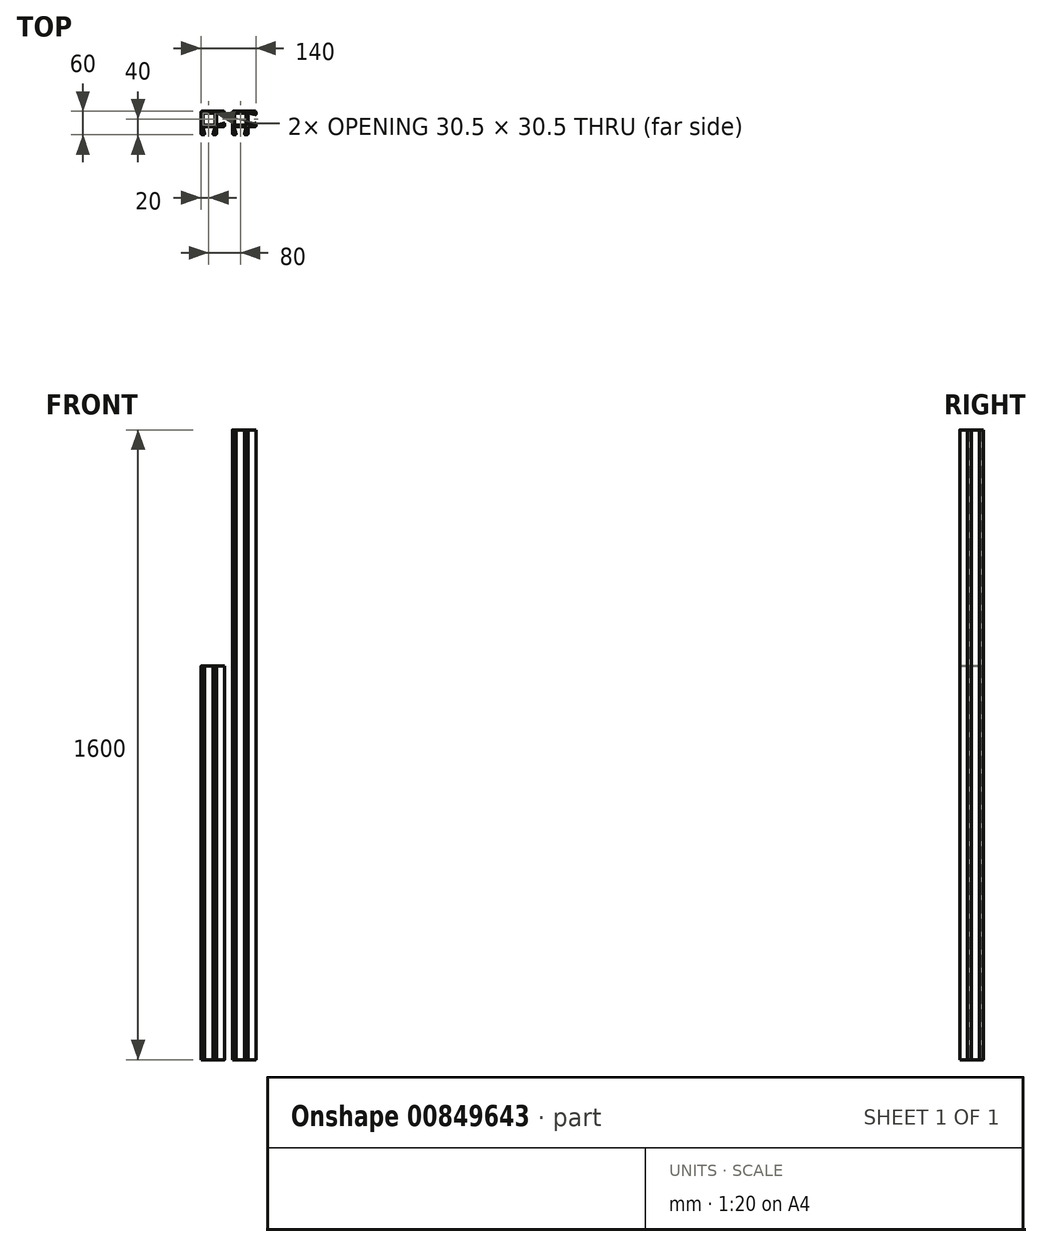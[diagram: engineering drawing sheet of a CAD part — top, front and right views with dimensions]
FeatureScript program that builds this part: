
annotation { "Feature Type Name" : "Feature", "Feature Type Description" : "" }
export const myFeature = defineFeature(function(context is Context, id is Id, definition is map)
    precondition{}
    {
        {
            var Q0;
            Q0=qCreatedBy(makeId("Top.planeOp"),FACE);
            var sketch = newSketch(context, id + "F0", { "sketchPlane" : qUnion([Q0])});
            skLineSegment(sketch, "E0", {"start": v(28.43, -0.67) * mm, "end": v(11.26, -5.27) * mm});
            skLineSegment(sketch, "E1", {"start": v(30, -6) * mm, "end": v(30, -1.88) * mm});
            skLineSegment(sketch, "E2", {"start": v(14, -10) * mm, "end": v(26, -10) * mm});
            skLineSegment(sketch, "E3", {"start": v(10, -26) * mm, "end": v(10, -14) * mm});
            skLineSegment(sketch, "E4", {"start": v(1.88, -30) * mm, "end": v(6, -30) * mm});
            skLineSegment(sketch, "E5", {"start": v(5.27, -11.26) * mm, "end": v(0.67, -28.43) * mm});
            skLineSegment(sketch, "E6", {"start": v(-9, -10) * mm, "end": v(4.3, -10) * mm});
            skLineSegment(sketch, "E7", {"start": v(-9.75, -9.64) * mm, "end": v(-9.25, -9.93) * mm});
            skLineSegment(sketch, "E8", {"start": v(-10.75, -9.93) * mm, "end": v(-10.25, -9.64) * mm});
            skLineSegment(sketch, "E9", {"start": v(-24.3, -10) * mm, "end": v(-11, -10) * mm});
            skLineSegment(sketch, "E10", {"start": v(-20.67, -28.43) * mm, "end": v(-25.27, -11.26) * mm});
            skLineSegment(sketch, "E11", {"start": v(-26, -30) * mm, "end": v(-21.88, -30) * mm});
            skLineSegment(sketch, "E12", {"start": v(-30, 26) * mm, "end": v(-30, -26) * mm});
            skLineSegment(sketch, "E13", {"start": v(26, 30) * mm, "end": v(-26, 30) * mm});
            skLineSegment(sketch, "E14", {"start": v(30, 21.88) * mm, "end": v(30, 26) * mm});
            skLineSegment(sketch, "E15", {"start": v(11.26, 25.27) * mm, "end": v(28.43, 20.67) * mm});
            skLineSegment(sketch, "E16", {"start": v(10, 11) * mm, "end": v(10, 24.3) * mm});
            skLineSegment(sketch, "E17", {"start": v(9.93, 10.75) * mm, "end": v(9.64, 10.25) * mm});
            skLineSegment(sketch, "E18", {"start": v(9.64, 9.75) * mm, "end": v(9.93, 9.25) * mm});
            skLineSegment(sketch, "E19", {"start": v(10, -4.3) * mm, "end": v(10, 9) * mm});
            skLineSegment(sketch, "E20", {"start": v(5.25, -4.75) * mm, "end": v(5.25, 24.75) * mm});
            skLineSegment(sketch, "E21", {"start": v(4.75, 25.25) * mm, "end": v(-24.75, 25.25) * mm});
            skLineSegment(sketch, "E22", {"start": v(-25.25, 24.75) * mm, "end": v(-25.25, -4.75) * mm});
            skLineSegment(sketch, "E23", {"start": v(-24.75, -5.25) * mm, "end": v(4.75, -5.25) * mm});
            skArc(sketch, "E24", {"start": v(10, -4.3) * mm, "mid": v(10.4, -5.1) * mm, "end": v(11.26, -5.27) * mm});
            skArc(sketch, "E25", {"start": v(30, -1.88) * mm, "mid": v(29.51, -0.89) * mm, "end": v(28.43, -0.67) * mm});
            skArc(sketch, "E26", {"start": v(26, -10) * mm, "mid": v(28.83, -8.83) * mm, "end": v(30, -6) * mm});
            skArc(sketch, "E27", {"start": v(14, -10) * mm, "mid": v(11.17, -11.17) * mm, "end": v(10, -14) * mm});
            skArc(sketch, "E28", {"start": v(6, -30) * mm, "mid": v(8.83, -28.83) * mm, "end": v(10, -26) * mm});
            skArc(sketch, "E29", {"start": v(0.67, -28.43) * mm, "mid": v(0.89, -29.51) * mm, "end": v(1.88, -30) * mm});
            skArc(sketch, "E30", {"start": v(5.27, -11.26) * mm, "mid": v(5.1, -10.4) * mm, "end": v(4.3, -10) * mm});
            skArc(sketch, "E31", {"start": v(-9.25, -9.93) * mm, "mid": v(-9.13, -9.98) * mm, "end": v(-9, -10) * mm});
            skArc(sketch, "E32", {"start": v(-9.75, -9.64) * mm, "mid": v(-10, -9.58) * mm, "end": v(-10.25, -9.64) * mm});
            skArc(sketch, "E33", {"start": v(-11, -10) * mm, "mid": v(-10.87, -9.98) * mm, "end": v(-10.75, -9.93) * mm});
            skArc(sketch, "E34", {"start": v(-24.3, -10) * mm, "mid": v(-25.1, -10.4) * mm, "end": v(-25.27, -11.26) * mm});
            skArc(sketch, "E35", {"start": v(-21.88, -30) * mm, "mid": v(-20.89, -29.51) * mm, "end": v(-20.67, -28.43) * mm});
            skArc(sketch, "E36", {"start": v(-30, -26) * mm, "mid": v(-28.83, -28.83) * mm, "end": v(-26, -30) * mm});
            skArc(sketch, "E37", {"start": v(-26, 30) * mm, "mid": v(-28.83, 28.83) * mm, "end": v(-30, 26) * mm});
            skArc(sketch, "E38", {"start": v(30, 26) * mm, "mid": v(28.83, 28.83) * mm, "end": v(26, 30) * mm});
            skArc(sketch, "E39", {"start": v(28.43, 20.67) * mm, "mid": v(29.51, 20.89) * mm, "end": v(30, 21.88) * mm});
            skArc(sketch, "E40", {"start": v(11.26, 25.27) * mm, "mid": v(10.4, 25.1) * mm, "end": v(10, 24.3) * mm});
            skArc(sketch, "E41", {"start": v(9.93, 10.75) * mm, "mid": v(9.98, 10.87) * mm, "end": v(10, 11) * mm});
            skArc(sketch, "E42", {"start": v(9.64, 10.25) * mm, "mid": v(9.58, 10) * mm, "end": v(9.64, 9.75) * mm});
            skArc(sketch, "E43", {"start": v(10, 9) * mm, "mid": v(9.98, 9.13) * mm, "end": v(9.93, 9.25) * mm});
            skArc(sketch, "E44", {"start": v(4.75, -5.25) * mm, "mid": v(5.1, -5.1) * mm, "end": v(5.25, -4.75) * mm});
            skArc(sketch, "E45", {"start": v(5.25, 24.75) * mm, "mid": v(5.1, 25.1) * mm, "end": v(4.75, 25.25) * mm});
            skArc(sketch, "E46", {"start": v(-24.75, 25.25) * mm, "mid": v(-25.1, 25.1) * mm, "end": v(-25.25, 24.75) * mm});
            skArc(sketch, "E47", {"start": v(-25.25, -4.75) * mm, "mid": v(-25.1, -5.1) * mm, "end": v(-24.75, -5.25) * mm});
            skLineSegment(sketch, "E48.1.0.0", {"start": v(108.43, -0.67) * mm, "end": v(91.26, -5.27) * mm});
            skLineSegment(sketch, "E48.1.0.1", {"start": v(94, -10) * mm, "end": v(106, -10) * mm});
            skLineSegment(sketch, "E48.1.0.2", {"start": v(55.25, -5.25) * mm, "end": v(84.75, -5.25) * mm});
            skLineSegment(sketch, "E48.1.0.3", {"start": v(54.75, 24.75) * mm, "end": v(54.75, -4.75) * mm});
            skLineSegment(sketch, "E48.1.0.4", {"start": v(84.75, 25.25) * mm, "end": v(55.25, 25.25) * mm});
            skLineSegment(sketch, "E48.1.0.5", {"start": v(71, -10) * mm, "end": v(84.3, -10) * mm});
            skLineSegment(sketch, "E48.1.0.6", {"start": v(85.25, -4.75) * mm, "end": v(85.25, 24.75) * mm});
            skLineSegment(sketch, "E48.1.0.7", {"start": v(50, 26) * mm, "end": v(50, -26) * mm});
            skLineSegment(sketch, "E48.1.0.8", {"start": v(91.26, 25.27) * mm, "end": v(108.43, 20.67) * mm});
            skLineSegment(sketch, "E48.1.0.9", {"start": v(106, 30) * mm, "end": v(54, 30) * mm});
            skLineSegment(sketch, "E48.1.0.10", {"start": v(85.27, -11.26) * mm, "end": v(80.67, -28.43) * mm});
            skArc(sketch, "E48.1.0.11", {"start": v(86, -30) * mm, "mid": v(88.83, -28.83) * mm, "end": v(90, -26) * mm});
            skArc(sketch, "E48.1.0.12", {"start": v(106, -10) * mm, "mid": v(108.83, -8.83) * mm, "end": v(110, -6) * mm});
            skLineSegment(sketch, "E48.1.0.13", {"start": v(90, -26) * mm, "end": v(90, -14) * mm});
            skArc(sketch, "E48.1.0.14", {"start": v(108.43, 20.67) * mm, "mid": v(109.51, 20.89) * mm, "end": v(110, 21.88) * mm});
            skArc(sketch, "E48.1.0.15", {"start": v(110, 26) * mm, "mid": v(108.83, 28.83) * mm, "end": v(106, 30) * mm});
            skArc(sketch, "E48.1.0.16", {"start": v(50, -26) * mm, "mid": v(51.17, -28.83) * mm, "end": v(54, -30) * mm});
            skLineSegment(sketch, "E48.1.0.17", {"start": v(110, 21.88) * mm, "end": v(110, 26) * mm});
            skArc(sketch, "E48.1.0.18", {"start": v(91.26, 25.27) * mm, "mid": v(90.4, 25.1) * mm, "end": v(90, 24.3) * mm});
            skArc(sketch, "E48.1.0.19", {"start": v(55.25, 25.25) * mm, "mid": v(54.9, 25.1) * mm, "end": v(54.75, 24.75) * mm});
            skArc(sketch, "E48.1.0.20", {"start": v(54, 30) * mm, "mid": v(51.17, 28.83) * mm, "end": v(50, 26) * mm});
            skLineSegment(sketch, "E48.1.0.21", {"start": v(59.33, -28.43) * mm, "end": v(54.73, -11.26) * mm});
            skLineSegment(sketch, "E48.1.0.22", {"start": v(54, -30) * mm, "end": v(58.12, -30) * mm});
            skArc(sketch, "E48.1.0.23", {"start": v(94, -10) * mm, "mid": v(91.17, -11.17) * mm, "end": v(90, -14) * mm});
            skArc(sketch, "E48.1.0.24", {"start": v(90, -4.3) * mm, "mid": v(90.4, -5.1) * mm, "end": v(91.26, -5.27) * mm});
            skArc(sketch, "E48.1.0.25", {"start": v(54.75, -4.75) * mm, "mid": v(54.9, -5.1) * mm, "end": v(55.25, -5.25) * mm});
            skArc(sketch, "E48.1.0.26", {"start": v(58.12, -30) * mm, "mid": v(59.11, -29.51) * mm, "end": v(59.33, -28.43) * mm});
            skLineSegment(sketch, "E48.1.0.27", {"start": v(90, -4.3) * mm, "end": v(90, 9) * mm});
            skArc(sketch, "E48.1.0.28", {"start": v(55.7, -10) * mm, "mid": v(54.9, -10.4) * mm, "end": v(54.73, -11.26) * mm});
            skLineSegment(sketch, "E48.1.0.29", {"start": v(55.7, -10) * mm, "end": v(69, -10) * mm});
            skLineSegment(sketch, "E48.1.0.30", {"start": v(90, 11) * mm, "end": v(90, 24.3) * mm});
            skArc(sketch, "E48.1.0.31", {"start": v(84.75, -5.25) * mm, "mid": v(85.1, -5.1) * mm, "end": v(85.25, -4.75) * mm});
            skArc(sketch, "E48.1.0.32", {"start": v(110, -1.88) * mm, "mid": v(109.51, -0.89) * mm, "end": v(108.43, -0.67) * mm});
            skLineSegment(sketch, "E48.1.0.33", {"start": v(110, -6) * mm, "end": v(110, -1.88) * mm});
            skLineSegment(sketch, "E48.1.0.34", {"start": v(81.88, -30) * mm, "end": v(86, -30) * mm});
            skArc(sketch, "E48.1.0.35", {"start": v(85.27, -11.26) * mm, "mid": v(85.1, -10.4) * mm, "end": v(84.3, -10) * mm});
            skArc(sketch, "E48.1.0.36", {"start": v(85.25, 24.75) * mm, "mid": v(85.1, 25.1) * mm, "end": v(84.75, 25.25) * mm});
            skArc(sketch, "E48.1.0.37", {"start": v(80.67, -28.43) * mm, "mid": v(80.89, -29.51) * mm, "end": v(81.88, -30) * mm});
            skLineSegment(sketch, "E48.1.0.38", {"start": v(69.25, -9.93) * mm, "end": v(69.75, -9.64) * mm});
            skArc(sketch, "E48.1.0.39", {"start": v(70.25, -9.64) * mm, "mid": v(70, -9.58) * mm, "end": v(69.75, -9.64) * mm});
            skArc(sketch, "E48.1.0.40", {"start": v(70.75, -9.93) * mm, "mid": v(70.87, -9.98) * mm, "end": v(71, -10) * mm});
            skLineSegment(sketch, "E48.1.0.41", {"start": v(89.64, 9.75) * mm, "end": v(89.93, 9.25) * mm});
            skArc(sketch, "E48.1.0.42", {"start": v(69, -10) * mm, "mid": v(69.13, -9.98) * mm, "end": v(69.25, -9.93) * mm});
            skLineSegment(sketch, "E48.1.0.43", {"start": v(89.93, 10.75) * mm, "end": v(89.64, 10.25) * mm});
            skArc(sketch, "E48.1.0.44", {"start": v(89.64, 10.25) * mm, "mid": v(89.58, 10) * mm, "end": v(89.64, 9.75) * mm});
            skArc(sketch, "E48.1.0.45", {"start": v(89.93, 10.75) * mm, "mid": v(89.98, 10.87) * mm, "end": v(90, 11) * mm});
            skLineSegment(sketch, "E48.1.0.46", {"start": v(70.25, -9.64) * mm, "end": v(70.75, -9.93) * mm});
            skArc(sketch, "E48.1.0.47", {"start": v(90, 9) * mm, "mid": v(89.98, 9.13) * mm, "end": v(89.93, 9.25) * mm});
            skLineSegment(sketch, "E48.2.0.0", {"start": v(188.43, -0.67) * mm, "end": v(171.26, -5.27) * mm});
            skLineSegment(sketch, "E48.2.0.1", {"start": v(174, -10) * mm, "end": v(186, -10) * mm});
            skLineSegment(sketch, "E48.2.0.2", {"start": v(135.25, -5.25) * mm, "end": v(164.75, -5.25) * mm});
            skLineSegment(sketch, "E48.2.0.3", {"start": v(134.75, 24.75) * mm, "end": v(134.75, -4.75) * mm});
            skLineSegment(sketch, "E48.2.0.4", {"start": v(164.75, 25.25) * mm, "end": v(135.25, 25.25) * mm});
            skLineSegment(sketch, "E48.2.0.5", {"start": v(151, -10) * mm, "end": v(164.3, -10) * mm});
            skLineSegment(sketch, "E48.2.0.6", {"start": v(165.25, -4.75) * mm, "end": v(165.25, 24.75) * mm});
            skLineSegment(sketch, "E48.2.0.7", {"start": v(130, 26) * mm, "end": v(130, -26) * mm});
            skLineSegment(sketch, "E48.2.0.8", {"start": v(171.26, 25.27) * mm, "end": v(188.43, 20.67) * mm});
            skLineSegment(sketch, "E48.2.0.9", {"start": v(186, 30) * mm, "end": v(134, 30) * mm});
            skLineSegment(sketch, "E48.2.0.10", {"start": v(165.27, -11.26) * mm, "end": v(160.67, -28.43) * mm});
            skArc(sketch, "E48.2.0.11", {"start": v(166, -30) * mm, "mid": v(168.83, -28.83) * mm, "end": v(170, -26) * mm});
            skArc(sketch, "E48.2.0.12", {"start": v(186, -10) * mm, "mid": v(188.83, -8.83) * mm, "end": v(190, -6) * mm});
            skLineSegment(sketch, "E48.2.0.13", {"start": v(170, -26) * mm, "end": v(170, -14) * mm});
            skArc(sketch, "E48.2.0.14", {"start": v(188.43, 20.67) * mm, "mid": v(189.51, 20.89) * mm, "end": v(190, 21.88) * mm});
            skArc(sketch, "E48.2.0.15", {"start": v(190, 26) * mm, "mid": v(188.83, 28.83) * mm, "end": v(186, 30) * mm});
            skArc(sketch, "E48.2.0.16", {"start": v(130, -26) * mm, "mid": v(131.17, -28.83) * mm, "end": v(134, -30) * mm});
            skLineSegment(sketch, "E48.2.0.17", {"start": v(190, 21.88) * mm, "end": v(190, 26) * mm});
            skArc(sketch, "E48.2.0.18", {"start": v(171.26, 25.27) * mm, "mid": v(170.4, 25.1) * mm, "end": v(170, 24.3) * mm});
            skArc(sketch, "E48.2.0.19", {"start": v(135.25, 25.25) * mm, "mid": v(134.9, 25.1) * mm, "end": v(134.75, 24.75) * mm});
            skArc(sketch, "E48.2.0.20", {"start": v(134, 30) * mm, "mid": v(131.17, 28.83) * mm, "end": v(130, 26) * mm});
            skLineSegment(sketch, "E48.2.0.21", {"start": v(139.33, -28.43) * mm, "end": v(134.73, -11.26) * mm});
            skLineSegment(sketch, "E48.2.0.22", {"start": v(134, -30) * mm, "end": v(138.12, -30) * mm});
            skArc(sketch, "E48.2.0.23", {"start": v(174, -10) * mm, "mid": v(171.17, -11.17) * mm, "end": v(170, -14) * mm});
            skArc(sketch, "E48.2.0.24", {"start": v(170, -4.3) * mm, "mid": v(170.4, -5.1) * mm, "end": v(171.26, -5.27) * mm});
            skArc(sketch, "E48.2.0.25", {"start": v(134.75, -4.75) * mm, "mid": v(134.9, -5.1) * mm, "end": v(135.25, -5.25) * mm});
            skArc(sketch, "E48.2.0.26", {"start": v(138.12, -30) * mm, "mid": v(139.11, -29.51) * mm, "end": v(139.33, -28.43) * mm});
            skLineSegment(sketch, "E48.2.0.27", {"start": v(170, -4.3) * mm, "end": v(170, 9) * mm});
            skArc(sketch, "E48.2.0.28", {"start": v(135.7, -10) * mm, "mid": v(134.9, -10.4) * mm, "end": v(134.73, -11.26) * mm});
            skLineSegment(sketch, "E48.2.0.29", {"start": v(135.7, -10) * mm, "end": v(149, -10) * mm});
            skLineSegment(sketch, "E48.2.0.30", {"start": v(170, 11) * mm, "end": v(170, 24.3) * mm});
            skArc(sketch, "E48.2.0.31", {"start": v(164.75, -5.25) * mm, "mid": v(165.1, -5.1) * mm, "end": v(165.25, -4.75) * mm});
            skArc(sketch, "E48.2.0.32", {"start": v(190, -1.88) * mm, "mid": v(189.51, -0.89) * mm, "end": v(188.43, -0.67) * mm});
            skLineSegment(sketch, "E48.2.0.33", {"start": v(190, -6) * mm, "end": v(190, -1.88) * mm});
            skLineSegment(sketch, "E48.2.0.34", {"start": v(161.88, -30) * mm, "end": v(166, -30) * mm});
            skArc(sketch, "E48.2.0.35", {"start": v(165.27, -11.26) * mm, "mid": v(165.1, -10.4) * mm, "end": v(164.3, -10) * mm});
            skArc(sketch, "E48.2.0.36", {"start": v(165.25, 24.75) * mm, "mid": v(165.1, 25.1) * mm, "end": v(164.75, 25.25) * mm});
            skArc(sketch, "E48.2.0.37", {"start": v(160.67, -28.43) * mm, "mid": v(160.89, -29.51) * mm, "end": v(161.88, -30) * mm});
            skLineSegment(sketch, "E48.2.0.38", {"start": v(149.25, -9.93) * mm, "end": v(149.75, -9.64) * mm});
            skArc(sketch, "E48.2.0.39", {"start": v(150.25, -9.64) * mm, "mid": v(150, -9.58) * mm, "end": v(149.75, -9.64) * mm});
            skArc(sketch, "E48.2.0.40", {"start": v(150.75, -9.93) * mm, "mid": v(150.87, -9.98) * mm, "end": v(151, -10) * mm});
            skLineSegment(sketch, "E48.2.0.41", {"start": v(169.64, 9.75) * mm, "end": v(169.93, 9.25) * mm});
            skArc(sketch, "E48.2.0.42", {"start": v(149, -10) * mm, "mid": v(149.13, -9.98) * mm, "end": v(149.25, -9.93) * mm});
            skLineSegment(sketch, "E48.2.0.43", {"start": v(169.93, 10.75) * mm, "end": v(169.64, 10.25) * mm});
            skArc(sketch, "E48.2.0.44", {"start": v(169.64, 10.25) * mm, "mid": v(169.58, 10) * mm, "end": v(169.64, 9.75) * mm});
            skArc(sketch, "E48.2.0.45", {"start": v(169.93, 10.75) * mm, "mid": v(169.98, 10.87) * mm, "end": v(170, 11) * mm});
            skLineSegment(sketch, "E48.2.0.46", {"start": v(150.25, -9.64) * mm, "end": v(150.75, -9.93) * mm});
            skArc(sketch, "E48.2.0.47", {"start": v(170, 9) * mm, "mid": v(169.98, 9.13) * mm, "end": v(169.93, 9.25) * mm});
            skLineSegment(sketch, "E48.3.0.0", {"start": v(268.43, -0.67) * mm, "end": v(251.26, -5.27) * mm});
            skLineSegment(sketch, "E48.3.0.1", {"start": v(254, -10) * mm, "end": v(266, -10) * mm});
            skLineSegment(sketch, "E48.3.0.2", {"start": v(215.25, -5.25) * mm, "end": v(244.75, -5.25) * mm});
            skLineSegment(sketch, "E48.3.0.3", {"start": v(214.75, 24.75) * mm, "end": v(214.75, -4.75) * mm});
            skLineSegment(sketch, "E48.3.0.4", {"start": v(244.75, 25.25) * mm, "end": v(215.25, 25.25) * mm});
            skLineSegment(sketch, "E48.3.0.5", {"start": v(231, -10) * mm, "end": v(244.3, -10) * mm});
            skLineSegment(sketch, "E48.3.0.6", {"start": v(245.25, -4.75) * mm, "end": v(245.25, 24.75) * mm});
            skLineSegment(sketch, "E48.3.0.7", {"start": v(210, 26) * mm, "end": v(210, -26) * mm});
            skLineSegment(sketch, "E48.3.0.8", {"start": v(251.26, 25.27) * mm, "end": v(268.43, 20.67) * mm});
            skLineSegment(sketch, "E48.3.0.9", {"start": v(266, 30) * mm, "end": v(214, 30) * mm});
            skLineSegment(sketch, "E48.3.0.10", {"start": v(245.27, -11.26) * mm, "end": v(240.67, -28.43) * mm});
            skArc(sketch, "E48.3.0.11", {"start": v(246, -30) * mm, "mid": v(248.83, -28.83) * mm, "end": v(250, -26) * mm});
            skArc(sketch, "E48.3.0.12", {"start": v(266, -10) * mm, "mid": v(268.83, -8.83) * mm, "end": v(270, -6) * mm});
            skLineSegment(sketch, "E48.3.0.13", {"start": v(250, -26) * mm, "end": v(250, -14) * mm});
            skArc(sketch, "E48.3.0.14", {"start": v(268.43, 20.67) * mm, "mid": v(269.51, 20.89) * mm, "end": v(270, 21.88) * mm});
            skArc(sketch, "E48.3.0.15", {"start": v(270, 26) * mm, "mid": v(268.83, 28.83) * mm, "end": v(266, 30) * mm});
            skArc(sketch, "E48.3.0.16", {"start": v(210, -26) * mm, "mid": v(211.17, -28.83) * mm, "end": v(214, -30) * mm});
            skLineSegment(sketch, "E48.3.0.17", {"start": v(270, 21.88) * mm, "end": v(270, 26) * mm});
            skArc(sketch, "E48.3.0.18", {"start": v(251.26, 25.27) * mm, "mid": v(250.4, 25.1) * mm, "end": v(250, 24.3) * mm});
            skArc(sketch, "E48.3.0.19", {"start": v(215.25, 25.25) * mm, "mid": v(214.9, 25.1) * mm, "end": v(214.75, 24.75) * mm});
            skArc(sketch, "E48.3.0.20", {"start": v(214, 30) * mm, "mid": v(211.17, 28.83) * mm, "end": v(210, 26) * mm});
            skLineSegment(sketch, "E48.3.0.21", {"start": v(219.33, -28.43) * mm, "end": v(214.73, -11.26) * mm});
            skLineSegment(sketch, "E48.3.0.22", {"start": v(214, -30) * mm, "end": v(218.12, -30) * mm});
            skArc(sketch, "E48.3.0.23", {"start": v(254, -10) * mm, "mid": v(251.17, -11.17) * mm, "end": v(250, -14) * mm});
            skArc(sketch, "E48.3.0.24", {"start": v(250, -4.3) * mm, "mid": v(250.4, -5.1) * mm, "end": v(251.26, -5.27) * mm});
            skArc(sketch, "E48.3.0.25", {"start": v(214.75, -4.75) * mm, "mid": v(214.9, -5.1) * mm, "end": v(215.25, -5.25) * mm});
            skArc(sketch, "E48.3.0.26", {"start": v(218.12, -30) * mm, "mid": v(219.11, -29.51) * mm, "end": v(219.33, -28.43) * mm});
            skLineSegment(sketch, "E48.3.0.27", {"start": v(250, -4.3) * mm, "end": v(250, 9) * mm});
            skArc(sketch, "E48.3.0.28", {"start": v(215.7, -10) * mm, "mid": v(214.9, -10.4) * mm, "end": v(214.73, -11.26) * mm});
            skLineSegment(sketch, "E48.3.0.29", {"start": v(215.7, -10) * mm, "end": v(229, -10) * mm});
            skLineSegment(sketch, "E48.3.0.30", {"start": v(250, 11) * mm, "end": v(250, 24.3) * mm});
            skArc(sketch, "E48.3.0.31", {"start": v(244.75, -5.25) * mm, "mid": v(245.1, -5.1) * mm, "end": v(245.25, -4.75) * mm});
            skArc(sketch, "E48.3.0.32", {"start": v(270, -1.88) * mm, "mid": v(269.51, -0.89) * mm, "end": v(268.43, -0.67) * mm});
            skLineSegment(sketch, "E48.3.0.33", {"start": v(270, -6) * mm, "end": v(270, -1.88) * mm});
            skLineSegment(sketch, "E48.3.0.34", {"start": v(241.88, -30) * mm, "end": v(246, -30) * mm});
            skArc(sketch, "E48.3.0.35", {"start": v(245.27, -11.26) * mm, "mid": v(245.1, -10.4) * mm, "end": v(244.3, -10) * mm});
            skArc(sketch, "E48.3.0.36", {"start": v(245.25, 24.75) * mm, "mid": v(245.1, 25.1) * mm, "end": v(244.75, 25.25) * mm});
            skArc(sketch, "E48.3.0.37", {"start": v(240.67, -28.43) * mm, "mid": v(240.89, -29.51) * mm, "end": v(241.88, -30) * mm});
            skLineSegment(sketch, "E48.3.0.38", {"start": v(229.25, -9.93) * mm, "end": v(229.75, -9.64) * mm});
            skArc(sketch, "E48.3.0.39", {"start": v(230.25, -9.64) * mm, "mid": v(230, -9.58) * mm, "end": v(229.75, -9.64) * mm});
            skArc(sketch, "E48.3.0.40", {"start": v(230.75, -9.93) * mm, "mid": v(230.87, -9.98) * mm, "end": v(231, -10) * mm});
            skLineSegment(sketch, "E48.3.0.41", {"start": v(249.64, 9.75) * mm, "end": v(249.93, 9.25) * mm});
            skArc(sketch, "E48.3.0.42", {"start": v(229, -10) * mm, "mid": v(229.13, -9.98) * mm, "end": v(229.25, -9.93) * mm});
            skLineSegment(sketch, "E48.3.0.43", {"start": v(249.93, 10.75) * mm, "end": v(249.64, 10.25) * mm});
            skArc(sketch, "E48.3.0.44", {"start": v(249.64, 10.25) * mm, "mid": v(249.58, 10) * mm, "end": v(249.64, 9.75) * mm});
            skArc(sketch, "E48.3.0.45", {"start": v(249.93, 10.75) * mm, "mid": v(249.98, 10.87) * mm, "end": v(250, 11) * mm});
            skLineSegment(sketch, "E48.3.0.46", {"start": v(230.25, -9.64) * mm, "end": v(230.75, -9.93) * mm});
            skArc(sketch, "E48.3.0.47", {"start": v(250, 9) * mm, "mid": v(249.98, 9.13) * mm, "end": v(249.93, 9.25) * mm});
            skLineSegment(sketch, "E48.4.0.0", {"start": v(348.43, -0.67) * mm, "end": v(331.26, -5.27) * mm});
            skLineSegment(sketch, "E48.4.0.1", {"start": v(334, -10) * mm, "end": v(346, -10) * mm});
            skLineSegment(sketch, "E48.4.0.2", {"start": v(295.25, -5.25) * mm, "end": v(324.75, -5.25) * mm});
            skLineSegment(sketch, "E48.4.0.3", {"start": v(294.75, 24.75) * mm, "end": v(294.75, -4.75) * mm});
            skLineSegment(sketch, "E48.4.0.4", {"start": v(324.75, 25.25) * mm, "end": v(295.25, 25.25) * mm});
            skLineSegment(sketch, "E48.4.0.5", {"start": v(311, -10) * mm, "end": v(324.3, -10) * mm});
            skLineSegment(sketch, "E48.4.0.6", {"start": v(325.25, -4.75) * mm, "end": v(325.25, 24.75) * mm});
            skLineSegment(sketch, "E48.4.0.7", {"start": v(290, 26) * mm, "end": v(290, -26) * mm});
            skLineSegment(sketch, "E48.4.0.8", {"start": v(331.26, 25.27) * mm, "end": v(348.43, 20.67) * mm});
            skLineSegment(sketch, "E48.4.0.9", {"start": v(346, 30) * mm, "end": v(294, 30) * mm});
            skLineSegment(sketch, "E48.4.0.10", {"start": v(325.27, -11.26) * mm, "end": v(320.67, -28.43) * mm});
            skArc(sketch, "E48.4.0.11", {"start": v(326, -30) * mm, "mid": v(328.83, -28.83) * mm, "end": v(330, -26) * mm});
            skArc(sketch, "E48.4.0.12", {"start": v(346, -10) * mm, "mid": v(348.83, -8.83) * mm, "end": v(350, -6) * mm});
            skLineSegment(sketch, "E48.4.0.13", {"start": v(330, -26) * mm, "end": v(330, -14) * mm});
            skArc(sketch, "E48.4.0.14", {"start": v(348.43, 20.67) * mm, "mid": v(349.51, 20.89) * mm, "end": v(350, 21.88) * mm});
            skArc(sketch, "E48.4.0.15", {"start": v(350, 26) * mm, "mid": v(348.83, 28.83) * mm, "end": v(346, 30) * mm});
            skArc(sketch, "E48.4.0.16", {"start": v(290, -26) * mm, "mid": v(291.17, -28.83) * mm, "end": v(294, -30) * mm});
            skLineSegment(sketch, "E48.4.0.17", {"start": v(350, 21.88) * mm, "end": v(350, 26) * mm});
            skArc(sketch, "E48.4.0.18", {"start": v(331.26, 25.27) * mm, "mid": v(330.4, 25.1) * mm, "end": v(330, 24.3) * mm});
            skArc(sketch, "E48.4.0.19", {"start": v(295.25, 25.25) * mm, "mid": v(294.9, 25.1) * mm, "end": v(294.75, 24.75) * mm});
            skArc(sketch, "E48.4.0.20", {"start": v(294, 30) * mm, "mid": v(291.17, 28.83) * mm, "end": v(290, 26) * mm});
            skLineSegment(sketch, "E48.4.0.21", {"start": v(299.33, -28.43) * mm, "end": v(294.73, -11.26) * mm});
            skLineSegment(sketch, "E48.4.0.22", {"start": v(294, -30) * mm, "end": v(298.12, -30) * mm});
            skArc(sketch, "E48.4.0.23", {"start": v(334, -10) * mm, "mid": v(331.17, -11.17) * mm, "end": v(330, -14) * mm});
            skArc(sketch, "E48.4.0.24", {"start": v(330, -4.3) * mm, "mid": v(330.4, -5.1) * mm, "end": v(331.26, -5.27) * mm});
            skArc(sketch, "E48.4.0.25", {"start": v(294.75, -4.75) * mm, "mid": v(294.9, -5.1) * mm, "end": v(295.25, -5.25) * mm});
            skArc(sketch, "E48.4.0.26", {"start": v(298.12, -30) * mm, "mid": v(299.11, -29.51) * mm, "end": v(299.33, -28.43) * mm});
            skLineSegment(sketch, "E48.4.0.27", {"start": v(330, -4.3) * mm, "end": v(330, 9) * mm});
            skArc(sketch, "E48.4.0.28", {"start": v(295.7, -10) * mm, "mid": v(294.9, -10.4) * mm, "end": v(294.73, -11.26) * mm});
            skLineSegment(sketch, "E48.4.0.29", {"start": v(295.7, -10) * mm, "end": v(309, -10) * mm});
            skLineSegment(sketch, "E48.4.0.30", {"start": v(330, 11) * mm, "end": v(330, 24.3) * mm});
            skArc(sketch, "E48.4.0.31", {"start": v(324.75, -5.25) * mm, "mid": v(325.1, -5.1) * mm, "end": v(325.25, -4.75) * mm});
            skArc(sketch, "E48.4.0.32", {"start": v(350, -1.88) * mm, "mid": v(349.51, -0.89) * mm, "end": v(348.43, -0.67) * mm});
            skLineSegment(sketch, "E48.4.0.33", {"start": v(350, -6) * mm, "end": v(350, -1.88) * mm});
            skLineSegment(sketch, "E48.4.0.34", {"start": v(321.88, -30) * mm, "end": v(326, -30) * mm});
            skArc(sketch, "E48.4.0.35", {"start": v(325.27, -11.26) * mm, "mid": v(325.1, -10.4) * mm, "end": v(324.3, -10) * mm});
            skArc(sketch, "E48.4.0.36", {"start": v(325.25, 24.75) * mm, "mid": v(325.1, 25.1) * mm, "end": v(324.75, 25.25) * mm});
            skArc(sketch, "E48.4.0.37", {"start": v(320.67, -28.43) * mm, "mid": v(320.89, -29.51) * mm, "end": v(321.88, -30) * mm});
            skLineSegment(sketch, "E48.4.0.38", {"start": v(309.25, -9.93) * mm, "end": v(309.75, -9.64) * mm});
            skArc(sketch, "E48.4.0.39", {"start": v(310.25, -9.64) * mm, "mid": v(310, -9.58) * mm, "end": v(309.75, -9.64) * mm});
            skArc(sketch, "E48.4.0.40", {"start": v(310.75, -9.93) * mm, "mid": v(310.87, -9.98) * mm, "end": v(311, -10) * mm});
            skLineSegment(sketch, "E48.4.0.41", {"start": v(329.64, 9.75) * mm, "end": v(329.93, 9.25) * mm});
            skArc(sketch, "E48.4.0.42", {"start": v(309, -10) * mm, "mid": v(309.13, -9.98) * mm, "end": v(309.25, -9.93) * mm});
            skLineSegment(sketch, "E48.4.0.43", {"start": v(329.93, 10.75) * mm, "end": v(329.64, 10.25) * mm});
            skArc(sketch, "E48.4.0.44", {"start": v(329.64, 10.25) * mm, "mid": v(329.58, 10) * mm, "end": v(329.64, 9.75) * mm});
            skArc(sketch, "E48.4.0.45", {"start": v(329.93, 10.75) * mm, "mid": v(329.98, 10.87) * mm, "end": v(330, 11) * mm});
            skLineSegment(sketch, "E48.4.0.46", {"start": v(310.25, -9.64) * mm, "end": v(310.75, -9.93) * mm});
            skArc(sketch, "E48.4.0.47", {"start": v(330, 9) * mm, "mid": v(329.98, 9.13) * mm, "end": v(329.93, 9.25) * mm});
            skLineSegment(sketch, "E48.5.0.0", {"start": v(428.43, -0.67) * mm, "end": v(411.26, -5.27) * mm});
            skLineSegment(sketch, "E48.5.0.1", {"start": v(414, -10) * mm, "end": v(426, -10) * mm});
            skLineSegment(sketch, "E48.5.0.2", {"start": v(375.25, -5.25) * mm, "end": v(404.75, -5.25) * mm});
            skLineSegment(sketch, "E48.5.0.3", {"start": v(374.75, 24.75) * mm, "end": v(374.75, -4.75) * mm});
            skLineSegment(sketch, "E48.5.0.4", {"start": v(404.75, 25.25) * mm, "end": v(375.25, 25.25) * mm});
            skLineSegment(sketch, "E48.5.0.5", {"start": v(391, -10) * mm, "end": v(404.3, -10) * mm});
            skLineSegment(sketch, "E48.5.0.6", {"start": v(405.25, -4.75) * mm, "end": v(405.25, 24.75) * mm});
            skLineSegment(sketch, "E48.5.0.7", {"start": v(370, 26) * mm, "end": v(370, -26) * mm});
            skLineSegment(sketch, "E48.5.0.8", {"start": v(411.26, 25.27) * mm, "end": v(428.43, 20.67) * mm});
            skLineSegment(sketch, "E48.5.0.9", {"start": v(426, 30) * mm, "end": v(374, 30) * mm});
            skLineSegment(sketch, "E48.5.0.10", {"start": v(405.27, -11.26) * mm, "end": v(400.67, -28.43) * mm});
            skArc(sketch, "E48.5.0.11", {"start": v(406, -30) * mm, "mid": v(408.83, -28.83) * mm, "end": v(410, -26) * mm});
            skArc(sketch, "E48.5.0.12", {"start": v(426, -10) * mm, "mid": v(428.83, -8.83) * mm, "end": v(430, -6) * mm});
            skLineSegment(sketch, "E48.5.0.13", {"start": v(410, -26) * mm, "end": v(410, -14) * mm});
            skArc(sketch, "E48.5.0.14", {"start": v(428.43, 20.67) * mm, "mid": v(429.51, 20.89) * mm, "end": v(430, 21.88) * mm});
            skArc(sketch, "E48.5.0.15", {"start": v(430, 26) * mm, "mid": v(428.83, 28.83) * mm, "end": v(426, 30) * mm});
            skArc(sketch, "E48.5.0.16", {"start": v(370, -26) * mm, "mid": v(371.17, -28.83) * mm, "end": v(374, -30) * mm});
            skLineSegment(sketch, "E48.5.0.17", {"start": v(430, 21.88) * mm, "end": v(430, 26) * mm});
            skArc(sketch, "E48.5.0.18", {"start": v(411.26, 25.27) * mm, "mid": v(410.4, 25.1) * mm, "end": v(410, 24.3) * mm});
            skArc(sketch, "E48.5.0.19", {"start": v(375.25, 25.25) * mm, "mid": v(374.9, 25.1) * mm, "end": v(374.75, 24.75) * mm});
            skArc(sketch, "E48.5.0.20", {"start": v(374, 30) * mm, "mid": v(371.17, 28.83) * mm, "end": v(370, 26) * mm});
            skLineSegment(sketch, "E48.5.0.21", {"start": v(379.33, -28.43) * mm, "end": v(374.73, -11.26) * mm});
            skLineSegment(sketch, "E48.5.0.22", {"start": v(374, -30) * mm, "end": v(378.12, -30) * mm});
            skArc(sketch, "E48.5.0.23", {"start": v(414, -10) * mm, "mid": v(411.17, -11.17) * mm, "end": v(410, -14) * mm});
            skArc(sketch, "E48.5.0.24", {"start": v(410, -4.3) * mm, "mid": v(410.4, -5.1) * mm, "end": v(411.26, -5.27) * mm});
            skArc(sketch, "E48.5.0.25", {"start": v(374.75, -4.75) * mm, "mid": v(374.9, -5.1) * mm, "end": v(375.25, -5.25) * mm});
            skArc(sketch, "E48.5.0.26", {"start": v(378.12, -30) * mm, "mid": v(379.11, -29.51) * mm, "end": v(379.33, -28.43) * mm});
            skLineSegment(sketch, "E48.5.0.27", {"start": v(410, -4.3) * mm, "end": v(410, 9) * mm});
            skArc(sketch, "E48.5.0.28", {"start": v(375.7, -10) * mm, "mid": v(374.9, -10.4) * mm, "end": v(374.73, -11.26) * mm});
            skLineSegment(sketch, "E48.5.0.29", {"start": v(375.7, -10) * mm, "end": v(389, -10) * mm});
            skLineSegment(sketch, "E48.5.0.30", {"start": v(410, 11) * mm, "end": v(410, 24.3) * mm});
            skArc(sketch, "E48.5.0.31", {"start": v(404.75, -5.25) * mm, "mid": v(405.1, -5.1) * mm, "end": v(405.25, -4.75) * mm});
            skArc(sketch, "E48.5.0.32", {"start": v(430, -1.88) * mm, "mid": v(429.51, -0.89) * mm, "end": v(428.43, -0.67) * mm});
            skLineSegment(sketch, "E48.5.0.33", {"start": v(430, -6) * mm, "end": v(430, -1.88) * mm});
            skLineSegment(sketch, "E48.5.0.34", {"start": v(401.88, -30) * mm, "end": v(406, -30) * mm});
            skArc(sketch, "E48.5.0.35", {"start": v(405.27, -11.26) * mm, "mid": v(405.1, -10.4) * mm, "end": v(404.3, -10) * mm});
            skArc(sketch, "E48.5.0.36", {"start": v(405.25, 24.75) * mm, "mid": v(405.1, 25.1) * mm, "end": v(404.75, 25.25) * mm});
            skArc(sketch, "E48.5.0.37", {"start": v(400.67, -28.43) * mm, "mid": v(400.89, -29.51) * mm, "end": v(401.88, -30) * mm});
            skLineSegment(sketch, "E48.5.0.38", {"start": v(389.25, -9.93) * mm, "end": v(389.75, -9.64) * mm});
            skArc(sketch, "E48.5.0.39", {"start": v(390.25, -9.64) * mm, "mid": v(390, -9.58) * mm, "end": v(389.75, -9.64) * mm});
            skArc(sketch, "E48.5.0.40", {"start": v(390.75, -9.93) * mm, "mid": v(390.87, -9.98) * mm, "end": v(391, -10) * mm});
            skLineSegment(sketch, "E48.5.0.41", {"start": v(409.64, 9.75) * mm, "end": v(409.93, 9.25) * mm});
            skArc(sketch, "E48.5.0.42", {"start": v(389, -10) * mm, "mid": v(389.13, -9.98) * mm, "end": v(389.25, -9.93) * mm});
            skLineSegment(sketch, "E48.5.0.43", {"start": v(409.93, 10.75) * mm, "end": v(409.64, 10.25) * mm});
            skArc(sketch, "E48.5.0.44", {"start": v(409.64, 10.25) * mm, "mid": v(409.58, 10) * mm, "end": v(409.64, 9.75) * mm});
            skArc(sketch, "E48.5.0.45", {"start": v(409.93, 10.75) * mm, "mid": v(409.98, 10.87) * mm, "end": v(410, 11) * mm});
            skLineSegment(sketch, "E48.5.0.46", {"start": v(390.25, -9.64) * mm, "end": v(390.75, -9.93) * mm});
            skArc(sketch, "E48.5.0.47", {"start": v(410, 9) * mm, "mid": v(409.98, 9.13) * mm, "end": v(409.93, 9.25) * mm});
            skLineSegment(sketch, "E48.6.0.0", {"start": v(508.43, -0.67) * mm, "end": v(491.26, -5.27) * mm});
            skLineSegment(sketch, "E48.6.0.1", {"start": v(494, -10) * mm, "end": v(506, -10) * mm});
            skLineSegment(sketch, "E48.6.0.2", {"start": v(455.25, -5.25) * mm, "end": v(484.75, -5.25) * mm});
            skLineSegment(sketch, "E48.6.0.3", {"start": v(454.75, 24.75) * mm, "end": v(454.75, -4.75) * mm});
            skLineSegment(sketch, "E48.6.0.4", {"start": v(484.75, 25.25) * mm, "end": v(455.25, 25.25) * mm});
            skLineSegment(sketch, "E48.6.0.5", {"start": v(471, -10) * mm, "end": v(484.3, -10) * mm});
            skLineSegment(sketch, "E48.6.0.6", {"start": v(485.25, -4.75) * mm, "end": v(485.25, 24.75) * mm});
            skLineSegment(sketch, "E48.6.0.7", {"start": v(450, 26) * mm, "end": v(450, -26) * mm});
            skLineSegment(sketch, "E48.6.0.8", {"start": v(491.26, 25.27) * mm, "end": v(508.43, 20.67) * mm});
            skLineSegment(sketch, "E48.6.0.9", {"start": v(506, 30) * mm, "end": v(454, 30) * mm});
            skLineSegment(sketch, "E48.6.0.10", {"start": v(485.27, -11.26) * mm, "end": v(480.67, -28.43) * mm});
            skArc(sketch, "E48.6.0.11", {"start": v(486, -30) * mm, "mid": v(488.83, -28.83) * mm, "end": v(490, -26) * mm});
            skArc(sketch, "E48.6.0.12", {"start": v(506, -10) * mm, "mid": v(508.83, -8.83) * mm, "end": v(510, -6) * mm});
            skLineSegment(sketch, "E48.6.0.13", {"start": v(490, -26) * mm, "end": v(490, -14) * mm});
            skArc(sketch, "E48.6.0.14", {"start": v(508.43, 20.67) * mm, "mid": v(509.51, 20.89) * mm, "end": v(510, 21.88) * mm});
            skArc(sketch, "E48.6.0.15", {"start": v(510, 26) * mm, "mid": v(508.83, 28.83) * mm, "end": v(506, 30) * mm});
            skArc(sketch, "E48.6.0.16", {"start": v(450, -26) * mm, "mid": v(451.17, -28.83) * mm, "end": v(454, -30) * mm});
            skLineSegment(sketch, "E48.6.0.17", {"start": v(510, 21.88) * mm, "end": v(510, 26) * mm});
            skArc(sketch, "E48.6.0.18", {"start": v(491.26, 25.27) * mm, "mid": v(490.4, 25.1) * mm, "end": v(490, 24.3) * mm});
            skArc(sketch, "E48.6.0.19", {"start": v(455.25, 25.25) * mm, "mid": v(454.9, 25.1) * mm, "end": v(454.75, 24.75) * mm});
            skArc(sketch, "E48.6.0.20", {"start": v(454, 30) * mm, "mid": v(451.17, 28.83) * mm, "end": v(450, 26) * mm});
            skLineSegment(sketch, "E48.6.0.21", {"start": v(459.33, -28.43) * mm, "end": v(454.73, -11.26) * mm});
            skLineSegment(sketch, "E48.6.0.22", {"start": v(454, -30) * mm, "end": v(458.12, -30) * mm});
            skArc(sketch, "E48.6.0.23", {"start": v(494, -10) * mm, "mid": v(491.17, -11.17) * mm, "end": v(490, -14) * mm});
            skArc(sketch, "E48.6.0.24", {"start": v(490, -4.3) * mm, "mid": v(490.4, -5.1) * mm, "end": v(491.26, -5.27) * mm});
            skArc(sketch, "E48.6.0.25", {"start": v(454.75, -4.75) * mm, "mid": v(454.9, -5.1) * mm, "end": v(455.25, -5.25) * mm});
            skArc(sketch, "E48.6.0.26", {"start": v(458.12, -30) * mm, "mid": v(459.11, -29.51) * mm, "end": v(459.33, -28.43) * mm});
            skLineSegment(sketch, "E48.6.0.27", {"start": v(490, -4.3) * mm, "end": v(490, 9) * mm});
            skArc(sketch, "E48.6.0.28", {"start": v(455.7, -10) * mm, "mid": v(454.9, -10.4) * mm, "end": v(454.73, -11.26) * mm});
            skLineSegment(sketch, "E48.6.0.29", {"start": v(455.7, -10) * mm, "end": v(469, -10) * mm});
            skLineSegment(sketch, "E48.6.0.30", {"start": v(490, 11) * mm, "end": v(490, 24.3) * mm});
            skArc(sketch, "E48.6.0.31", {"start": v(484.75, -5.25) * mm, "mid": v(485.1, -5.1) * mm, "end": v(485.25, -4.75) * mm});
            skArc(sketch, "E48.6.0.32", {"start": v(510, -1.88) * mm, "mid": v(509.51, -0.89) * mm, "end": v(508.43, -0.67) * mm});
            skLineSegment(sketch, "E48.6.0.33", {"start": v(510, -6) * mm, "end": v(510, -1.88) * mm});
            skLineSegment(sketch, "E48.6.0.34", {"start": v(481.88, -30) * mm, "end": v(486, -30) * mm});
            skArc(sketch, "E48.6.0.35", {"start": v(485.27, -11.26) * mm, "mid": v(485.1, -10.4) * mm, "end": v(484.3, -10) * mm});
            skArc(sketch, "E48.6.0.36", {"start": v(485.25, 24.75) * mm, "mid": v(485.1, 25.1) * mm, "end": v(484.75, 25.25) * mm});
            skArc(sketch, "E48.6.0.37", {"start": v(480.67, -28.43) * mm, "mid": v(480.89, -29.51) * mm, "end": v(481.88, -30) * mm});
            skLineSegment(sketch, "E48.6.0.38", {"start": v(469.25, -9.93) * mm, "end": v(469.75, -9.64) * mm});
            skArc(sketch, "E48.6.0.39", {"start": v(470.25, -9.64) * mm, "mid": v(470, -9.58) * mm, "end": v(469.75, -9.64) * mm});
            skArc(sketch, "E48.6.0.40", {"start": v(470.75, -9.93) * mm, "mid": v(470.87, -9.98) * mm, "end": v(471, -10) * mm});
            skLineSegment(sketch, "E48.6.0.41", {"start": v(489.64, 9.75) * mm, "end": v(489.93, 9.25) * mm});
            skArc(sketch, "E48.6.0.42", {"start": v(469, -10) * mm, "mid": v(469.13, -9.98) * mm, "end": v(469.25, -9.93) * mm});
            skLineSegment(sketch, "E48.6.0.43", {"start": v(489.93, 10.75) * mm, "end": v(489.64, 10.25) * mm});
            skArc(sketch, "E48.6.0.44", {"start": v(489.64, 10.25) * mm, "mid": v(489.58, 10) * mm, "end": v(489.64, 9.75) * mm});
            skArc(sketch, "E48.6.0.45", {"start": v(489.93, 10.75) * mm, "mid": v(489.98, 10.87) * mm, "end": v(490, 11) * mm});
            skLineSegment(sketch, "E48.6.0.46", {"start": v(470.25, -9.64) * mm, "end": v(470.75, -9.93) * mm});
            skArc(sketch, "E48.6.0.47", {"start": v(490, 9) * mm, "mid": v(489.98, 9.13) * mm, "end": v(489.93, 9.25) * mm});
            skLineSegment(sketch, "E48.7.0.0", {"start": v(588.43, -0.67) * mm, "end": v(571.26, -5.27) * mm});
            skLineSegment(sketch, "E48.7.0.1", {"start": v(574, -10) * mm, "end": v(586, -10) * mm});
            skLineSegment(sketch, "E48.7.0.2", {"start": v(535.25, -5.25) * mm, "end": v(564.75, -5.25) * mm});
            skLineSegment(sketch, "E48.7.0.3", {"start": v(534.75, 24.75) * mm, "end": v(534.75, -4.75) * mm});
            skLineSegment(sketch, "E48.7.0.4", {"start": v(564.75, 25.25) * mm, "end": v(535.25, 25.25) * mm});
            skLineSegment(sketch, "E48.7.0.5", {"start": v(551, -10) * mm, "end": v(564.3, -10) * mm});
            skLineSegment(sketch, "E48.7.0.6", {"start": v(565.25, -4.75) * mm, "end": v(565.25, 24.75) * mm});
            skLineSegment(sketch, "E48.7.0.7", {"start": v(530, 26) * mm, "end": v(530, -26) * mm});
            skLineSegment(sketch, "E48.7.0.8", {"start": v(571.26, 25.27) * mm, "end": v(588.43, 20.67) * mm});
            skLineSegment(sketch, "E48.7.0.9", {"start": v(586, 30) * mm, "end": v(534, 30) * mm});
            skLineSegment(sketch, "E48.7.0.10", {"start": v(565.27, -11.26) * mm, "end": v(560.67, -28.43) * mm});
            skArc(sketch, "E48.7.0.11", {"start": v(566, -30) * mm, "mid": v(568.83, -28.83) * mm, "end": v(570, -26) * mm});
            skArc(sketch, "E48.7.0.12", {"start": v(586, -10) * mm, "mid": v(588.83, -8.83) * mm, "end": v(590, -6) * mm});
            skLineSegment(sketch, "E48.7.0.13", {"start": v(570, -26) * mm, "end": v(570, -14) * mm});
            skArc(sketch, "E48.7.0.14", {"start": v(588.43, 20.67) * mm, "mid": v(589.51, 20.89) * mm, "end": v(590, 21.88) * mm});
            skArc(sketch, "E48.7.0.15", {"start": v(590, 26) * mm, "mid": v(588.83, 28.83) * mm, "end": v(586, 30) * mm});
            skArc(sketch, "E48.7.0.16", {"start": v(530, -26) * mm, "mid": v(531.17, -28.83) * mm, "end": v(534, -30) * mm});
            skLineSegment(sketch, "E48.7.0.17", {"start": v(590, 21.88) * mm, "end": v(590, 26) * mm});
            skArc(sketch, "E48.7.0.18", {"start": v(571.26, 25.27) * mm, "mid": v(570.4, 25.1) * mm, "end": v(570, 24.3) * mm});
            skArc(sketch, "E48.7.0.19", {"start": v(535.25, 25.25) * mm, "mid": v(534.9, 25.1) * mm, "end": v(534.75, 24.75) * mm});
            skArc(sketch, "E48.7.0.20", {"start": v(534, 30) * mm, "mid": v(531.17, 28.83) * mm, "end": v(530, 26) * mm});
            skLineSegment(sketch, "E48.7.0.21", {"start": v(539.33, -28.43) * mm, "end": v(534.73, -11.26) * mm});
            skLineSegment(sketch, "E48.7.0.22", {"start": v(534, -30) * mm, "end": v(538.12, -30) * mm});
            skArc(sketch, "E48.7.0.23", {"start": v(574, -10) * mm, "mid": v(571.17, -11.17) * mm, "end": v(570, -14) * mm});
            skArc(sketch, "E48.7.0.24", {"start": v(570, -4.3) * mm, "mid": v(570.4, -5.1) * mm, "end": v(571.26, -5.27) * mm});
            skArc(sketch, "E48.7.0.25", {"start": v(534.75, -4.75) * mm, "mid": v(534.9, -5.1) * mm, "end": v(535.25, -5.25) * mm});
            skArc(sketch, "E48.7.0.26", {"start": v(538.12, -30) * mm, "mid": v(539.11, -29.51) * mm, "end": v(539.33, -28.43) * mm});
            skLineSegment(sketch, "E48.7.0.27", {"start": v(570, -4.3) * mm, "end": v(570, 9) * mm});
            skArc(sketch, "E48.7.0.28", {"start": v(535.7, -10) * mm, "mid": v(534.9, -10.4) * mm, "end": v(534.73, -11.26) * mm});
            skLineSegment(sketch, "E48.7.0.29", {"start": v(535.7, -10) * mm, "end": v(549, -10) * mm});
            skLineSegment(sketch, "E48.7.0.30", {"start": v(570, 11) * mm, "end": v(570, 24.3) * mm});
            skArc(sketch, "E48.7.0.31", {"start": v(564.75, -5.25) * mm, "mid": v(565.1, -5.1) * mm, "end": v(565.25, -4.75) * mm});
            skArc(sketch, "E48.7.0.32", {"start": v(590, -1.88) * mm, "mid": v(589.51, -0.89) * mm, "end": v(588.43, -0.67) * mm});
            skLineSegment(sketch, "E48.7.0.33", {"start": v(590, -6) * mm, "end": v(590, -1.88) * mm});
            skLineSegment(sketch, "E48.7.0.34", {"start": v(561.88, -30) * mm, "end": v(566, -30) * mm});
            skArc(sketch, "E48.7.0.35", {"start": v(565.27, -11.26) * mm, "mid": v(565.1, -10.4) * mm, "end": v(564.3, -10) * mm});
            skArc(sketch, "E48.7.0.36", {"start": v(565.25, 24.75) * mm, "mid": v(565.1, 25.1) * mm, "end": v(564.75, 25.25) * mm});
            skArc(sketch, "E48.7.0.37", {"start": v(560.67, -28.43) * mm, "mid": v(560.89, -29.51) * mm, "end": v(561.88, -30) * mm});
            skLineSegment(sketch, "E48.7.0.38", {"start": v(549.25, -9.93) * mm, "end": v(549.75, -9.64) * mm});
            skArc(sketch, "E48.7.0.39", {"start": v(550.25, -9.64) * mm, "mid": v(550, -9.58) * mm, "end": v(549.75, -9.64) * mm});
            skArc(sketch, "E48.7.0.40", {"start": v(550.75, -9.93) * mm, "mid": v(550.87, -9.98) * mm, "end": v(551, -10) * mm});
            skLineSegment(sketch, "E48.7.0.41", {"start": v(569.64, 9.75) * mm, "end": v(569.93, 9.25) * mm});
            skArc(sketch, "E48.7.0.42", {"start": v(549, -10) * mm, "mid": v(549.13, -9.98) * mm, "end": v(549.25, -9.93) * mm});
            skLineSegment(sketch, "E48.7.0.43", {"start": v(569.93, 10.75) * mm, "end": v(569.64, 10.25) * mm});
            skArc(sketch, "E48.7.0.44", {"start": v(569.64, 10.25) * mm, "mid": v(569.58, 10) * mm, "end": v(569.64, 9.75) * mm});
            skArc(sketch, "E48.7.0.45", {"start": v(569.93, 10.75) * mm, "mid": v(569.98, 10.87) * mm, "end": v(570, 11) * mm});
            skLineSegment(sketch, "E48.7.0.46", {"start": v(550.25, -9.64) * mm, "end": v(550.75, -9.93) * mm});
            skArc(sketch, "E48.7.0.47", {"start": v(570, 9) * mm, "mid": v(569.98, 9.13) * mm, "end": v(569.93, 9.25) * mm});
            skLineSegment(sketch, "E48.8.0.0", {"start": v(668.43, -0.67) * mm, "end": v(651.26, -5.27) * mm});
            skLineSegment(sketch, "E48.8.0.1", {"start": v(654, -10) * mm, "end": v(666, -10) * mm});
            skLineSegment(sketch, "E48.8.0.2", {"start": v(615.25, -5.25) * mm, "end": v(644.75, -5.25) * mm});
            skLineSegment(sketch, "E48.8.0.3", {"start": v(614.75, 24.75) * mm, "end": v(614.75, -4.75) * mm});
            skLineSegment(sketch, "E48.8.0.4", {"start": v(644.75, 25.25) * mm, "end": v(615.25, 25.25) * mm});
            skLineSegment(sketch, "E48.8.0.5", {"start": v(631, -10) * mm, "end": v(644.3, -10) * mm});
            skLineSegment(sketch, "E48.8.0.6", {"start": v(645.25, -4.75) * mm, "end": v(645.25, 24.75) * mm});
            skLineSegment(sketch, "E48.8.0.7", {"start": v(610, 26) * mm, "end": v(610, -26) * mm});
            skLineSegment(sketch, "E48.8.0.8", {"start": v(651.26, 25.27) * mm, "end": v(668.43, 20.67) * mm});
            skLineSegment(sketch, "E48.8.0.9", {"start": v(666, 30) * mm, "end": v(614, 30) * mm});
            skLineSegment(sketch, "E48.8.0.10", {"start": v(645.27, -11.26) * mm, "end": v(640.67, -28.43) * mm});
            skArc(sketch, "E48.8.0.11", {"start": v(646, -30) * mm, "mid": v(648.83, -28.83) * mm, "end": v(650, -26) * mm});
            skArc(sketch, "E48.8.0.12", {"start": v(666, -10) * mm, "mid": v(668.83, -8.83) * mm, "end": v(670, -6) * mm});
            skLineSegment(sketch, "E48.8.0.13", {"start": v(650, -26) * mm, "end": v(650, -14) * mm});
            skArc(sketch, "E48.8.0.14", {"start": v(668.43, 20.67) * mm, "mid": v(669.51, 20.89) * mm, "end": v(670, 21.88) * mm});
            skArc(sketch, "E48.8.0.15", {"start": v(670, 26) * mm, "mid": v(668.83, 28.83) * mm, "end": v(666, 30) * mm});
            skArc(sketch, "E48.8.0.16", {"start": v(610, -26) * mm, "mid": v(611.17, -28.83) * mm, "end": v(614, -30) * mm});
            skLineSegment(sketch, "E48.8.0.17", {"start": v(670, 21.88) * mm, "end": v(670, 26) * mm});
            skArc(sketch, "E48.8.0.18", {"start": v(651.26, 25.27) * mm, "mid": v(650.4, 25.1) * mm, "end": v(650, 24.3) * mm});
            skArc(sketch, "E48.8.0.19", {"start": v(615.25, 25.25) * mm, "mid": v(614.9, 25.1) * mm, "end": v(614.75, 24.75) * mm});
            skArc(sketch, "E48.8.0.20", {"start": v(614, 30) * mm, "mid": v(611.17, 28.83) * mm, "end": v(610, 26) * mm});
            skLineSegment(sketch, "E48.8.0.21", {"start": v(619.33, -28.43) * mm, "end": v(614.73, -11.26) * mm});
            skLineSegment(sketch, "E48.8.0.22", {"start": v(614, -30) * mm, "end": v(618.12, -30) * mm});
            skArc(sketch, "E48.8.0.23", {"start": v(654, -10) * mm, "mid": v(651.17, -11.17) * mm, "end": v(650, -14) * mm});
            skArc(sketch, "E48.8.0.24", {"start": v(650, -4.3) * mm, "mid": v(650.4, -5.1) * mm, "end": v(651.26, -5.27) * mm});
            skArc(sketch, "E48.8.0.25", {"start": v(614.75, -4.75) * mm, "mid": v(614.9, -5.1) * mm, "end": v(615.25, -5.25) * mm});
            skArc(sketch, "E48.8.0.26", {"start": v(618.12, -30) * mm, "mid": v(619.11, -29.51) * mm, "end": v(619.33, -28.43) * mm});
            skLineSegment(sketch, "E48.8.0.27", {"start": v(650, -4.3) * mm, "end": v(650, 9) * mm});
            skArc(sketch, "E48.8.0.28", {"start": v(615.7, -10) * mm, "mid": v(614.9, -10.4) * mm, "end": v(614.73, -11.26) * mm});
            skLineSegment(sketch, "E48.8.0.29", {"start": v(615.7, -10) * mm, "end": v(629, -10) * mm});
            skLineSegment(sketch, "E48.8.0.30", {"start": v(650, 11) * mm, "end": v(650, 24.3) * mm});
            skArc(sketch, "E48.8.0.31", {"start": v(644.75, -5.25) * mm, "mid": v(645.1, -5.1) * mm, "end": v(645.25, -4.75) * mm});
            skArc(sketch, "E48.8.0.32", {"start": v(670, -1.88) * mm, "mid": v(669.51, -0.89) * mm, "end": v(668.43, -0.67) * mm});
            skLineSegment(sketch, "E48.8.0.33", {"start": v(670, -6) * mm, "end": v(670, -1.88) * mm});
            skLineSegment(sketch, "E48.8.0.34", {"start": v(641.88, -30) * mm, "end": v(646, -30) * mm});
            skArc(sketch, "E48.8.0.35", {"start": v(645.27, -11.26) * mm, "mid": v(645.1, -10.4) * mm, "end": v(644.3, -10) * mm});
            skArc(sketch, "E48.8.0.36", {"start": v(645.25, 24.75) * mm, "mid": v(645.1, 25.1) * mm, "end": v(644.75, 25.25) * mm});
            skArc(sketch, "E48.8.0.37", {"start": v(640.67, -28.43) * mm, "mid": v(640.89, -29.51) * mm, "end": v(641.88, -30) * mm});
            skLineSegment(sketch, "E48.8.0.38", {"start": v(629.25, -9.93) * mm, "end": v(629.75, -9.64) * mm});
            skArc(sketch, "E48.8.0.39", {"start": v(630.25, -9.64) * mm, "mid": v(630, -9.58) * mm, "end": v(629.75, -9.64) * mm});
            skArc(sketch, "E48.8.0.40", {"start": v(630.75, -9.93) * mm, "mid": v(630.87, -9.98) * mm, "end": v(631, -10) * mm});
            skLineSegment(sketch, "E48.8.0.41", {"start": v(649.64, 9.75) * mm, "end": v(649.93, 9.25) * mm});
            skArc(sketch, "E48.8.0.42", {"start": v(629, -10) * mm, "mid": v(629.13, -9.98) * mm, "end": v(629.25, -9.93) * mm});
            skLineSegment(sketch, "E48.8.0.43", {"start": v(649.93, 10.75) * mm, "end": v(649.64, 10.25) * mm});
            skArc(sketch, "E48.8.0.44", {"start": v(649.64, 10.25) * mm, "mid": v(649.58, 10) * mm, "end": v(649.64, 9.75) * mm});
            skArc(sketch, "E48.8.0.45", {"start": v(649.93, 10.75) * mm, "mid": v(649.98, 10.87) * mm, "end": v(650, 11) * mm});
            skLineSegment(sketch, "E48.8.0.46", {"start": v(630.25, -9.64) * mm, "end": v(630.75, -9.93) * mm});
            skArc(sketch, "E48.8.0.47", {"start": v(650, 9) * mm, "mid": v(649.98, 9.13) * mm, "end": v(649.93, 9.25) * mm});
            skLineSegment(sketch, "E48.9.0.0", {"start": v(748.43, -0.67) * mm, "end": v(731.26, -5.27) * mm});
            skLineSegment(sketch, "E48.9.0.1", {"start": v(734, -10) * mm, "end": v(746, -10) * mm});
            skLineSegment(sketch, "E48.9.0.2", {"start": v(695.25, -5.25) * mm, "end": v(724.75, -5.25) * mm});
            skLineSegment(sketch, "E48.9.0.3", {"start": v(694.75, 24.75) * mm, "end": v(694.75, -4.75) * mm});
            skLineSegment(sketch, "E48.9.0.4", {"start": v(724.75, 25.25) * mm, "end": v(695.25, 25.25) * mm});
            skLineSegment(sketch, "E48.9.0.5", {"start": v(711, -10) * mm, "end": v(724.3, -10) * mm});
            skLineSegment(sketch, "E48.9.0.6", {"start": v(725.25, -4.75) * mm, "end": v(725.25, 24.75) * mm});
            skLineSegment(sketch, "E48.9.0.7", {"start": v(690, 26) * mm, "end": v(690, -26) * mm});
            skLineSegment(sketch, "E48.9.0.8", {"start": v(731.26, 25.27) * mm, "end": v(748.43, 20.67) * mm});
            skLineSegment(sketch, "E48.9.0.9", {"start": v(746, 30) * mm, "end": v(694, 30) * mm});
            skLineSegment(sketch, "E48.9.0.10", {"start": v(725.27, -11.26) * mm, "end": v(720.67, -28.43) * mm});
            skArc(sketch, "E48.9.0.11", {"start": v(726, -30) * mm, "mid": v(728.83, -28.83) * mm, "end": v(730, -26) * mm});
            skArc(sketch, "E48.9.0.12", {"start": v(746, -10) * mm, "mid": v(748.83, -8.83) * mm, "end": v(750, -6) * mm});
            skLineSegment(sketch, "E48.9.0.13", {"start": v(730, -26) * mm, "end": v(730, -14) * mm});
            skArc(sketch, "E48.9.0.14", {"start": v(748.43, 20.67) * mm, "mid": v(749.51, 20.89) * mm, "end": v(750, 21.88) * mm});
            skArc(sketch, "E48.9.0.15", {"start": v(750, 26) * mm, "mid": v(748.83, 28.83) * mm, "end": v(746, 30) * mm});
            skArc(sketch, "E48.9.0.16", {"start": v(690, -26) * mm, "mid": v(691.17, -28.83) * mm, "end": v(694, -30) * mm});
            skLineSegment(sketch, "E48.9.0.17", {"start": v(750, 21.88) * mm, "end": v(750, 26) * mm});
            skArc(sketch, "E48.9.0.18", {"start": v(731.26, 25.27) * mm, "mid": v(730.4, 25.1) * mm, "end": v(730, 24.3) * mm});
            skArc(sketch, "E48.9.0.19", {"start": v(695.25, 25.25) * mm, "mid": v(694.9, 25.1) * mm, "end": v(694.75, 24.75) * mm});
            skArc(sketch, "E48.9.0.20", {"start": v(694, 30) * mm, "mid": v(691.17, 28.83) * mm, "end": v(690, 26) * mm});
            skLineSegment(sketch, "E48.9.0.21", {"start": v(699.33, -28.43) * mm, "end": v(694.73, -11.26) * mm});
            skLineSegment(sketch, "E48.9.0.22", {"start": v(694, -30) * mm, "end": v(698.12, -30) * mm});
            skArc(sketch, "E48.9.0.23", {"start": v(734, -10) * mm, "mid": v(731.17, -11.17) * mm, "end": v(730, -14) * mm});
            skArc(sketch, "E48.9.0.24", {"start": v(730, -4.3) * mm, "mid": v(730.4, -5.1) * mm, "end": v(731.26, -5.27) * mm});
            skArc(sketch, "E48.9.0.25", {"start": v(694.75, -4.75) * mm, "mid": v(694.9, -5.1) * mm, "end": v(695.25, -5.25) * mm});
            skArc(sketch, "E48.9.0.26", {"start": v(698.12, -30) * mm, "mid": v(699.11, -29.51) * mm, "end": v(699.33, -28.43) * mm});
            skLineSegment(sketch, "E48.9.0.27", {"start": v(730, -4.3) * mm, "end": v(730, 9) * mm});
            skArc(sketch, "E48.9.0.28", {"start": v(695.7, -10) * mm, "mid": v(694.9, -10.4) * mm, "end": v(694.73, -11.26) * mm});
            skLineSegment(sketch, "E48.9.0.29", {"start": v(695.7, -10) * mm, "end": v(709, -10) * mm});
            skLineSegment(sketch, "E48.9.0.30", {"start": v(730, 11) * mm, "end": v(730, 24.3) * mm});
            skArc(sketch, "E48.9.0.31", {"start": v(724.75, -5.25) * mm, "mid": v(725.1, -5.1) * mm, "end": v(725.25, -4.75) * mm});
            skArc(sketch, "E48.9.0.32", {"start": v(750, -1.88) * mm, "mid": v(749.51, -0.89) * mm, "end": v(748.43, -0.67) * mm});
            skLineSegment(sketch, "E48.9.0.33", {"start": v(750, -6) * mm, "end": v(750, -1.88) * mm});
            skLineSegment(sketch, "E48.9.0.34", {"start": v(721.88, -30) * mm, "end": v(726, -30) * mm});
            skArc(sketch, "E48.9.0.35", {"start": v(725.27, -11.26) * mm, "mid": v(725.1, -10.4) * mm, "end": v(724.3, -10) * mm});
            skArc(sketch, "E48.9.0.36", {"start": v(725.25, 24.75) * mm, "mid": v(725.1, 25.1) * mm, "end": v(724.75, 25.25) * mm});
            skArc(sketch, "E48.9.0.37", {"start": v(720.67, -28.43) * mm, "mid": v(720.89, -29.51) * mm, "end": v(721.88, -30) * mm});
            skLineSegment(sketch, "E48.9.0.38", {"start": v(709.25, -9.93) * mm, "end": v(709.75, -9.64) * mm});
            skArc(sketch, "E48.9.0.39", {"start": v(710.25, -9.64) * mm, "mid": v(710, -9.58) * mm, "end": v(709.75, -9.64) * mm});
            skArc(sketch, "E48.9.0.40", {"start": v(710.75, -9.93) * mm, "mid": v(710.87, -9.98) * mm, "end": v(711, -10) * mm});
            skLineSegment(sketch, "E48.9.0.41", {"start": v(729.64, 9.75) * mm, "end": v(729.93, 9.25) * mm});
            skArc(sketch, "E48.9.0.42", {"start": v(709, -10) * mm, "mid": v(709.13, -9.98) * mm, "end": v(709.25, -9.93) * mm});
            skLineSegment(sketch, "E48.9.0.43", {"start": v(729.93, 10.75) * mm, "end": v(729.64, 10.25) * mm});
            skArc(sketch, "E48.9.0.44", {"start": v(729.64, 10.25) * mm, "mid": v(729.58, 10) * mm, "end": v(729.64, 9.75) * mm});
            skArc(sketch, "E48.9.0.45", {"start": v(729.93, 10.75) * mm, "mid": v(729.98, 10.87) * mm, "end": v(730, 11) * mm});
            skLineSegment(sketch, "E48.9.0.46", {"start": v(710.25, -9.64) * mm, "end": v(710.75, -9.93) * mm});
            skArc(sketch, "E48.9.0.47", {"start": v(730, 9) * mm, "mid": v(729.98, 9.13) * mm, "end": v(729.93, 9.25) * mm});
            skLineSegment(sketch, "E48.direction1", {"start": v(-26, -30) * mm, "end": v(54, -30) * mm, "construction": true});
            skSolve(sketch);
        }
        {
            var Q0;
            Q0=makeQuery(id+"F0.imprint","IMPRINT",FACE,{"disambiguationData":[TD([[makeQuery(id+"F0.imprint","IMPRINT",EDGE,{"derivedFrom":sQuery(id+"F0.wireOp",EDGE,"E0")}),1.0]])]});
            extrude(context, id + "F1", {"entities" : qUnion([Q0]), "depth" : 1000 * mm, "offsetDistance" : 25 * mm});
        }
        {
            var Q0;
            Q0=makeQuery(id+"F0.imprint","IMPRINT",FACE,{"disambiguationData":[TD([[makeQuery(id+"F0.imprint","IMPRINT",EDGE,{"derivedFrom":sQuery(id+"F0.wireOp",EDGE,"E48.1.0.0")}),1.0]])]});
            extrude(context, id + "F2", {"entities" : qUnion([Q0]), "depth" : 1600 * mm, "offsetDistance" : 25 * mm});
        }
    });
